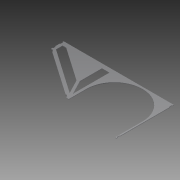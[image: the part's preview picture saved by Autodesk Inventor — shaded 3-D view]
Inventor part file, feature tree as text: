
AUTODESK INVENTOR PART (.ipt)
format: ipt  version: 2013 (Build 170138000, 138)  size: 139,776 bytes
history: native  units: in
note: dims shown in document units (in); Inventor stores cm internally (conversion verified against a paired STEP export)
features: extrude x4, sketch x4
ambient origin geometry x8: Origin, YZ Plane, XZ Plane, XY Plane, X Axis, Y Axis, Z Axis, Center Point
feature tree (8):
  extrude  "Extrusion2"  Depth=12.0in
  extrude  "Extrusion3"  Depth=5.75in
  extrude  "Extrusion4"  Depth=11.5in
  extrude  "Extrusion5"  Depth=0.25in
  sketch  "Sketch1"  dims[d0=22.0in d2=12.0in]
  sketch  "Sketch2"  dims[d3=11.25in d5=5.75in]
  sketch  "Sketch3"  dims[d8=0.125in d9=0.0in d10=11.5in]
  sketch  "Sketch4"  dims[d14=2.5in d15=0.25in d16=0.5in d17=0.5in d18=0.25in d19=0.125in d20=0.0in d21=0.5in d22=0.25in d23=0.25in d24=0.5in d25=0.125in d26=0.0in d27=0.5in d28=0.5in d29=0.25in d30=10.0in d31=0.125in d32=0.0in d33=9.5in d34=5.5in d37=0.25in]
